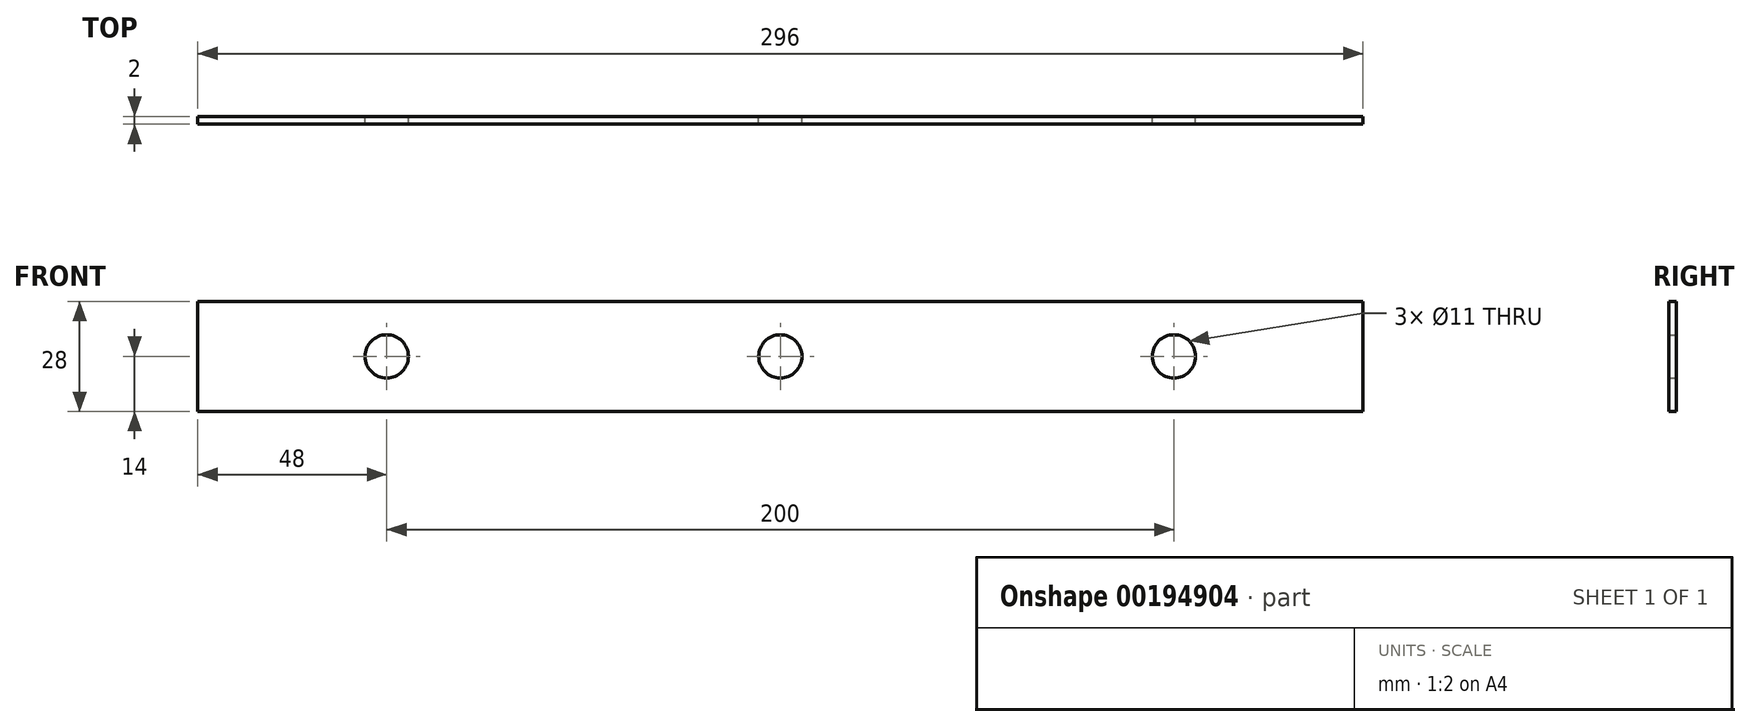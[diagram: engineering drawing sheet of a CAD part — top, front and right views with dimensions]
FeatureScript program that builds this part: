
annotation { "Feature Type Name" : "Feature", "Feature Type Description" : "" }
export const myFeature = defineFeature(function(context is Context, id is Id, definition is map)
    precondition{}
    {
        {
            var Q0;
            Q0=qCreatedBy(makeId("Front.planeOp"),FACE);
            var sketch = newSketch(context, id + "F0", { "sketchPlane" : qUnion([Q0])});
            skLineSegment(sketch, "E0.bottom", {"start": v(148, 14) * mm, "end": v(-148, 14) * mm});
            skLineSegment(sketch, "E0.top", {"start": v(148, -14) * mm, "end": v(-148, -14) * mm});
            skLineSegment(sketch, "E0.left", {"start": v(148, 14) * mm, "end": v(148, -14) * mm});
            skLineSegment(sketch, "E0.right", {"start": v(-148, 14) * mm, "end": v(-148, -14) * mm});
            skPoint(sketch, "E0.middle", {"position": v(0, 0) * mm});
            skCircle(sketch, "E1", {"center": v(-100, 0) * mm, "radius": 5.5 * mm});
            skCircle(sketch, "E2", {"center": v(0, 0) * mm, "radius": 5.5 * mm});
            skCircle(sketch, "E3", {"center": v(100, 0) * mm, "radius": 5.5 * mm});
            skSolve(sketch);
        }
        {
            var Q0;
            Q0 = qSketchRegion(id + "F0", true);
            extrude(context, id + "F1", {"entities" : qUnion([Q0]), "depth" : 2 * mm});
        }
    });
